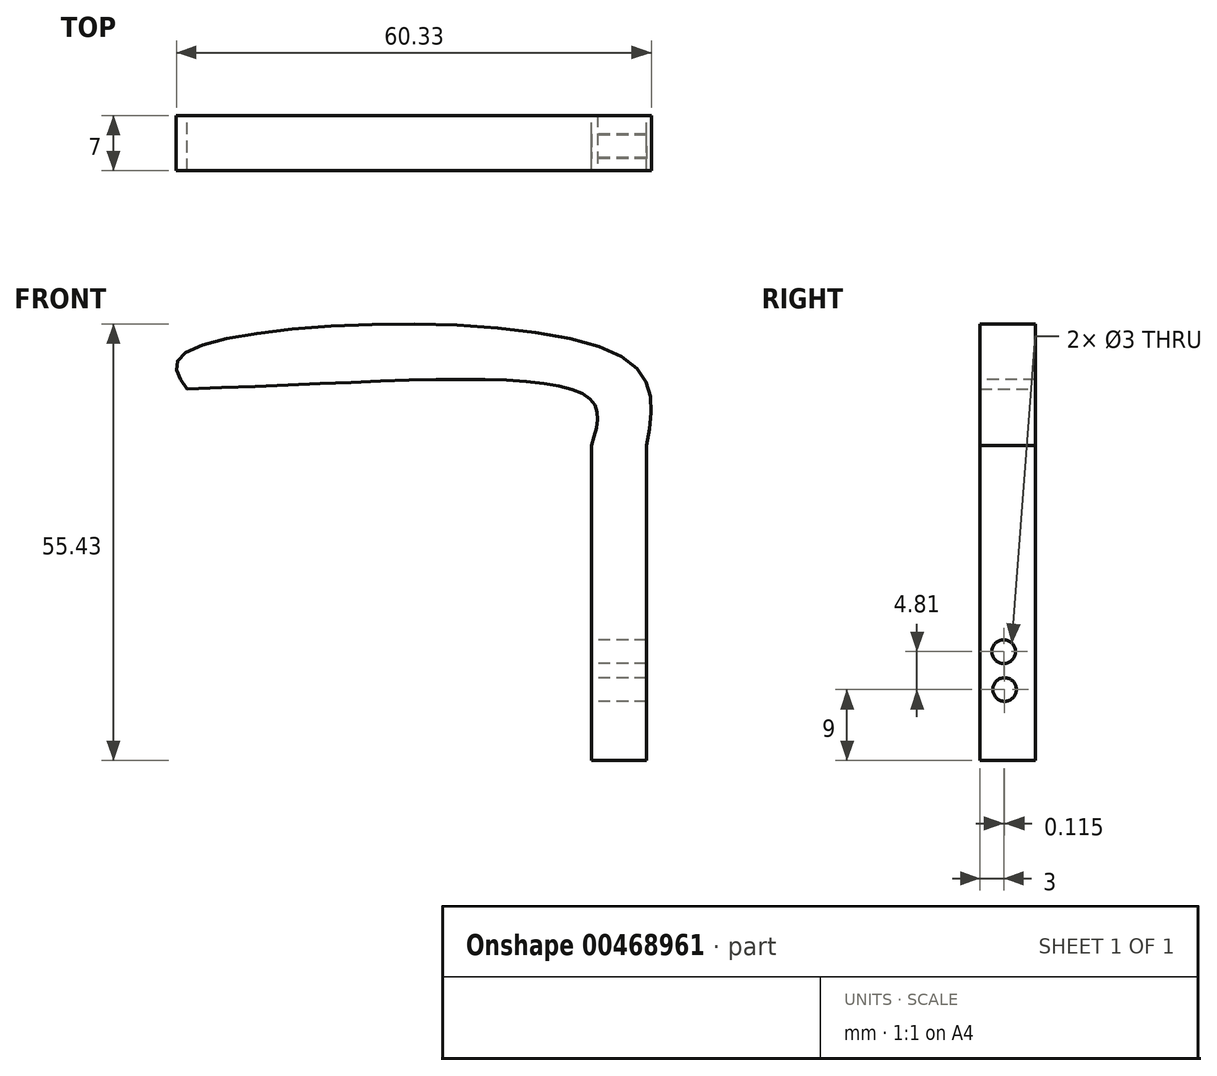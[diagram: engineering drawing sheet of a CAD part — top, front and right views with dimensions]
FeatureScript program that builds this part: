
annotation { "Feature Type Name" : "Feature", "Feature Type Description" : "" }
export const myFeature = defineFeature(function(context is Context, id is Id, definition is map)
    precondition{}
    {
        {
            var Q0;
            Q0=qCreatedBy(makeId("Front.planeOp"),FACE);
            var sketch = newSketch(context, id + "F0", { "sketchPlane" : qUnion([Q0])});
            skLineSegment(sketch, "E0.bottom", {"start": v(-7, 40) * mm, "end": v(0, 40) * mm});
            skLineSegment(sketch, "E0.top", {"start": v(-7, 0) * mm, "end": v(0, 0) * mm});
            skLineSegment(sketch, "E0.left", {"start": v(-7, 40) * mm, "end": v(-7, 0) * mm});
            skLineSegment(sketch, "E0.right", {"start": v(0, 40) * mm, "end": v(0, 0) * mm});
            skPoint(sketch, "E1.1.internal.snap0", {"position": v(-3.5, 40) * mm});
            skFitSpline(sketch, "E2", {"points": [v(-7, 40) * mm, v(-7, 45.76) * mm, v(-58.33, 47.19) * mm], "startDerivative": vector(8.94, 26.06) * mm, "endDerivative": vector(-101.2, -3.34) * mm});
            skPoint(sketch, "E1.1.internal.orphan", {"position": v(-3.5, 51.48) * mm});
            skFitSpline(sketch, "E3", {"points": [v(0, 40) * mm, v(-3.5, 51.48) * mm, v(-58.95, 51.48) * mm, v(-58.33, 47.19) * mm], "startDerivative": vector(9.4, 49.04) * mm, "endDerivative": vector(20.16, -28.32) * mm});
            skSolve(sketch);
        }
        {
            var Q0;
            {var subQ0=sQuery(id+"F0.wireOp",EDGE,"E0.bottom");Q0=makeQuery(id+"F0.imprint","IMPRINT",FACE,{"disambiguationData":[TD([[makeQuery(id+"F0.imprint","IMPRINT",EDGE,{"derivedFrom":subQ0}),1.0]])]});}
            var Q1;
            Q1=makeQuery(id+"F0.imprint","IMPRINT",FACE,{"disambiguationData":[TD([[makeQuery(id+"F0.imprint","IMPRINT",EDGE,{"derivedFrom":sQuery(id+"F0.wireOp",EDGE,"E0.bottom")}),-1.0]])]});
            extrude(context, id + "F1", {"entities" : qUnion([Q0, Q1]), "depth" : 7 * mm, "offsetDistance" : 25 * mm});
        }
        {
            var Q0;
            Q0=makeQuery(id+"F1.opExtrude","SWEPT_FACE",FACE,{"disambiguationData":[OSD([sQuery(id+"F0.wireOp",EDGE,"E0.left")])]});
            var sketch = newSketch(context, id + "F2", { "sketchPlane" : qUnion([Q0])});
            skCircle(sketch, "E4", {"center": v(4, 13.8) * mm, "radius": 1.5 * mm});
            skCircle(sketch, "E5", {"center": v(3.89, 9) * mm, "radius": 1.5 * mm});
            skSolve(sketch);
        }
        {
            var Q0;
            Q0=makeQuery(id+"F2.imprint","IMPRINT",FACE,{"disambiguationData":[TD([[makeQuery(id+"F2.imprint","IMPRINT",EDGE,{"derivedFrom":sQuery(id+"F2.wireOp",EDGE,"E4")}),1.0]])]});
            var Q1;
            Q1=makeQuery(id+"F2.imprint","IMPRINT",FACE,{"disambiguationData":[TD([[makeQuery(id+"F2.imprint","IMPRINT",EDGE,{"derivedFrom":sQuery(id+"F2.wireOp",EDGE,"E5")}),1.0]])]});
            extrude(context, id + "F3", {"entities" : qUnion([Q0, Q1]), "operationType" : NewBodyOperationType.REMOVE, "endBound" : BoundingType.THROUGH_ALL, "oppositeDirection" : true, "depth" : 25 * mm, "offsetDistance" : 25 * mm});
        }
    });
